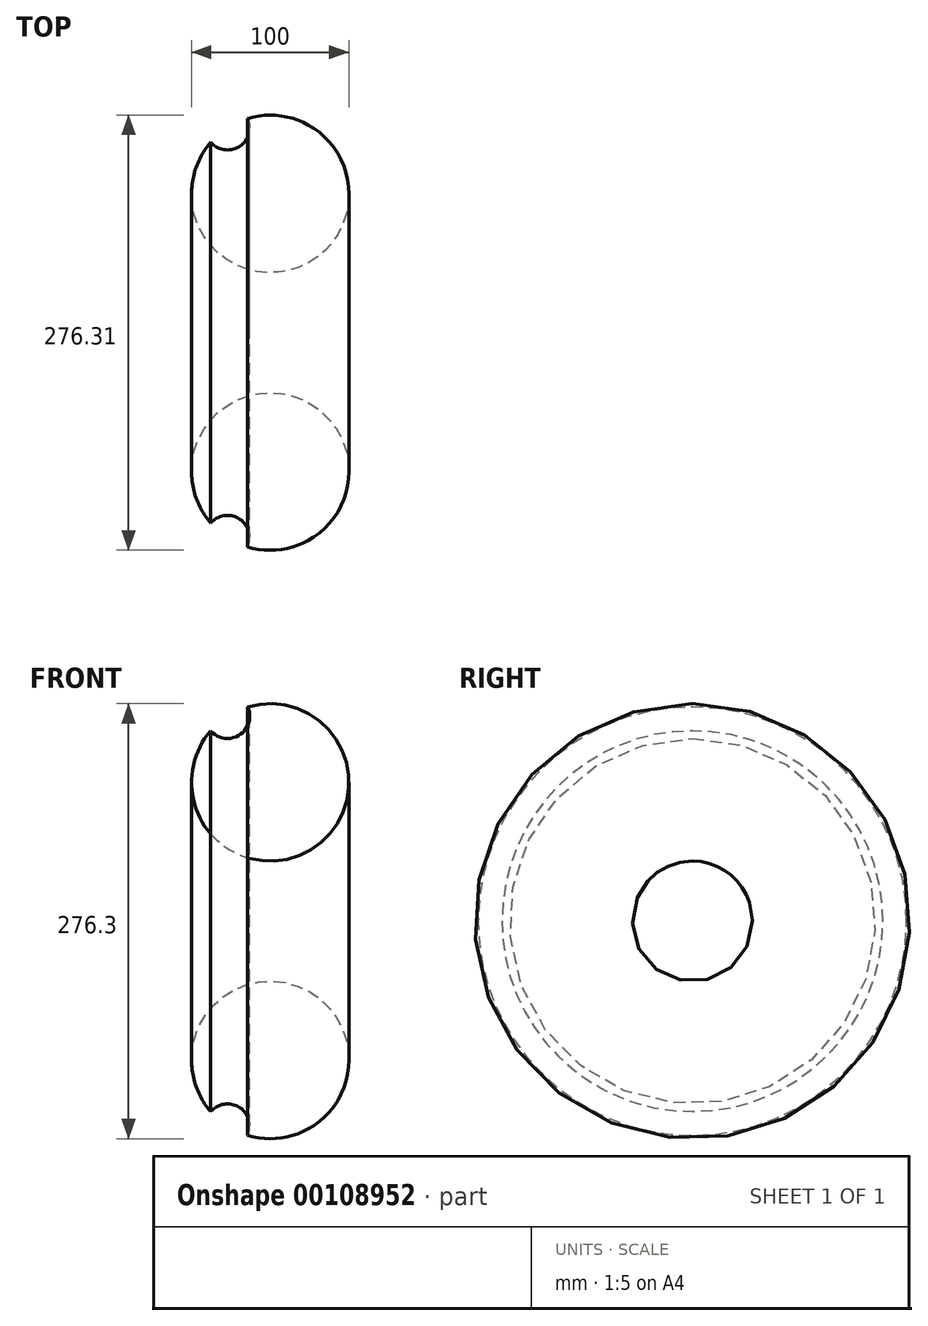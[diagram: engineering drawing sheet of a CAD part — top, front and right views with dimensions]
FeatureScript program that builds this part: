
annotation { "Feature Type Name" : "Feature", "Feature Type Description" : "" }
export const myFeature = defineFeature(function(context is Context, id is Id, definition is map)
    precondition{}
    {
        {
            var Q0;
            Q0=qCreatedBy(makeId("Top.planeOp"),FACE);
            var sketch = newSketch(context, id + "F0", { "sketchPlane" : qUnion([Q0])});
            skCircle(sketch, "E0", {"center": v(0, 0) * mm, "radius": 50 * mm});
            skCircle(sketch, "E1", {"center": v(-27.11, 42.01) * mm, "radius": 14.1 * mm});
            skLineSegment(sketch, "E2.bottom", {"start": v(-45.57, -88.15) * mm, "end": v(54.43, -88.15) * mm});
            skLineSegment(sketch, "E2.top", {"start": v(-45.57, -188.15) * mm, "end": v(54.43, -188.15) * mm});
            skLineSegment(sketch, "E2.left", {"start": v(-45.57, -88.15) * mm, "end": v(-45.57, -188.15) * mm});
            skLineSegment(sketch, "E2.right", {"start": v(54.43, -88.15) * mm, "end": v(54.43, -188.15) * mm});
            skLineSegment(sketch, "E3", {"start": v(-50, 0) * mm, "end": v(-113.24, -67.8) * mm});
            skLineSegment(sketch, "E4", {"start": v(-113.24, -67.8) * mm, "end": v(-45.57, -88.15) * mm});
            skLineSegment(sketch, "E5", {"start": v(0, -50) * mm, "end": v(-45.57, -88.15) * mm});
            skSolve(sketch);
        }
        {
            var Q0;
            {var subQ0=sQuery(id+"F0.wireOp",EDGE,"E1");var subQ1=sQuery(id+"F0.wireOp",EDGE,"E0");var subQ2=makeQuery(id+"F0.imprint","INTERSECT",VERTEX,{"disambiguationData":[OD(0.0)],"derivedFrom":[subQ1,subQ0]});Q0=makeQuery(id+"F0.imprint","IMPRINT",FACE,{"disambiguationData":[TD([[makeQuery(id+"F0.imprint","IMPRINT",EDGE,{"disambiguationData":[TD([[subQ2,-1.0]])],"derivedFrom":subQ1}),1.0]])]});}
            var Q1;
            Q1=sQuery(id+"F0.wireOp",EDGE,"E2.bottom");
            revolve(context, id + "F1", {"entities" : qUnion([Q0]), "axis" : qUnion([Q1]), "revolveType" : RevolveType.FULL});
        }
    });
